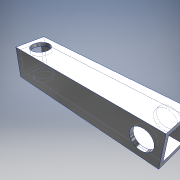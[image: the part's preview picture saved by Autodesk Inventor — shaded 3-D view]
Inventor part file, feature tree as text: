
AUTODESK INVENTOR PART (.ipt)
format: ipt  version: 2019 (Build 230136000, 136)  size: 124,416 bytes
history: native  units: in
note: dims shown in document units (in); Inventor stores cm internally (conversion verified against a paired STEP export)
features: extrude x3, sketch x3
ambient origin geometry x8: Origin, YZ Plane, XZ Plane, XY Plane, X Axis, Y Axis, Z Axis, Center Point
bodies: Solid1 (feature_tree)
feature tree (6):
  extrude  "Extrusion1"  Depth=1.0in
  extrude  "Extrusion2"  Depth=5.0in
  extrude  "Extrusion3"  Depth=5.0in TaperAngle=0.0deg
  sketch  "Sketch1"  dims[d0=0.125in d1=1.0in]
  sketch  "Sketch2"  dims[d2=5.0in d3=0.0in d4=0.625in]
  sketch  "Sketch3"  dims[d5=0.5in d6=5.0in d7=0.0in d8=0.5in d9=0.625in d10=5.0in d11=0.0in]
